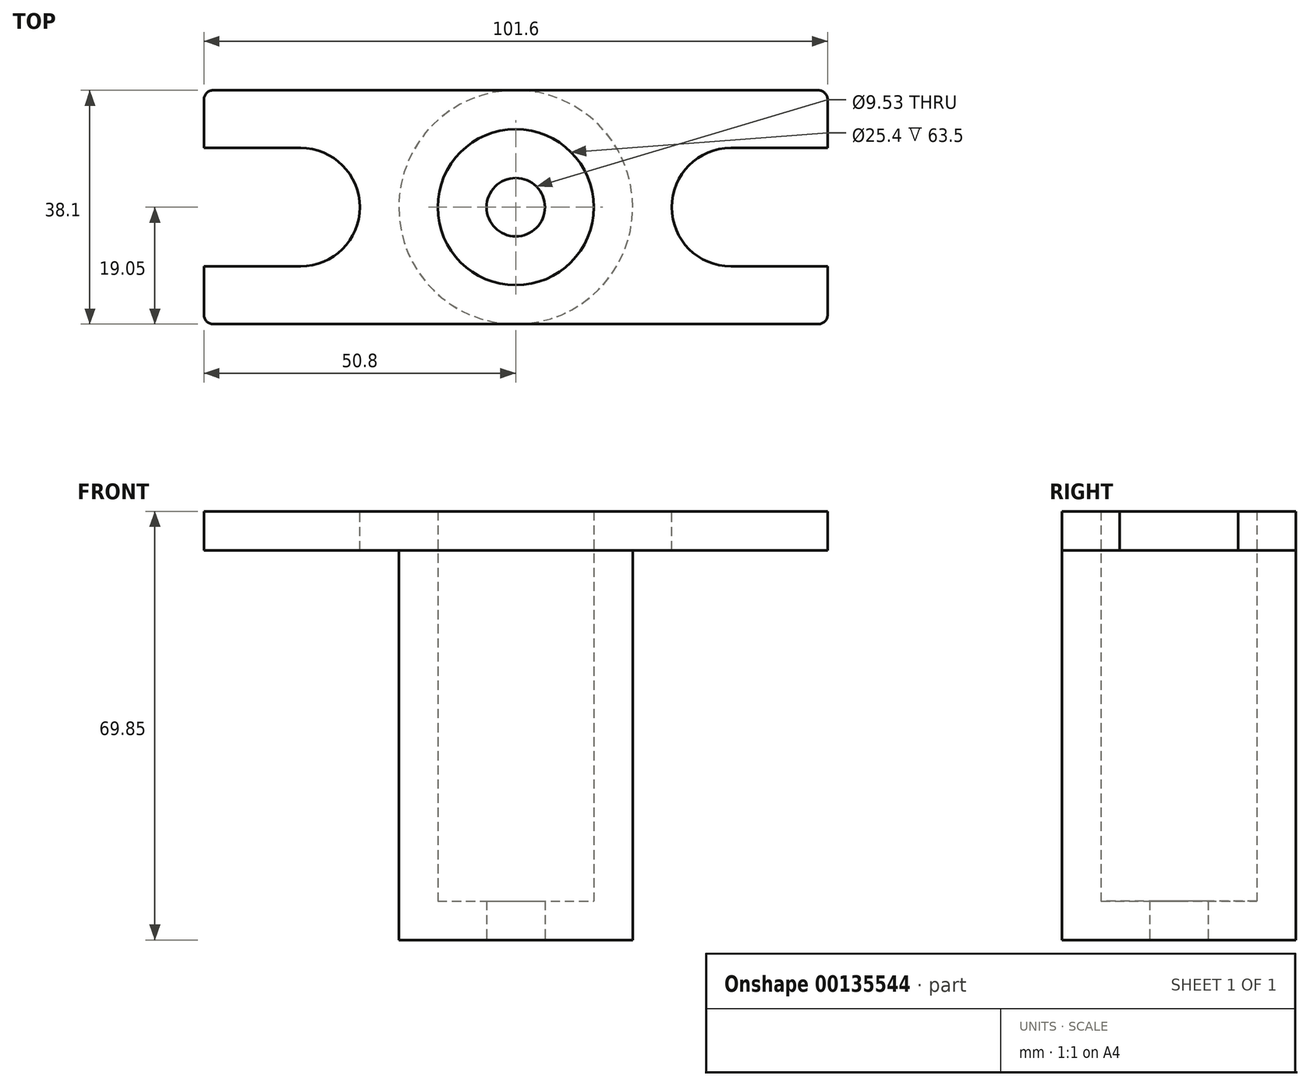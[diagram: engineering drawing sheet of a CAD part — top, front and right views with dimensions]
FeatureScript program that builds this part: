
annotation { "Feature Type Name" : "Feature", "Feature Type Description" : "" }
export const myFeature = defineFeature(function(context is Context, id is Id, definition is map)
    precondition{}
    {
        {
            var Q0;
            Q0=qCreatedBy(makeId("Front.planeOp"),FACE);
            var sketch = newSketch(context, id + "F0", { "sketchPlane" : qUnion([Q0])});
            skLineSegment(sketch, "E0", {"start": v(0, 0) * mm, "end": v(0, 62.9) * mm, "construction": true});
            skLineSegment(sketch, "E1", {"start": v(-4.76, 0) * mm, "end": v(-19.05, 0) * mm});
            skLineSegment(sketch, "E2", {"start": v(-19.05, 0) * mm, "end": v(-19.05, 69.85) * mm});
            skLineSegment(sketch, "E3", {"start": v(-19.05, 69.85) * mm, "end": v(-12.7, 69.85) * mm});
            skLineSegment(sketch, "E4", {"start": v(-12.7, 69.85) * mm, "end": v(-12.7, 6.35) * mm});
            skLineSegment(sketch, "E5", {"start": v(-12.7, 6.35) * mm, "end": v(-4.76, 6.35) * mm});
            skLineSegment(sketch, "E6", {"start": v(-4.76, 6.35) * mm, "end": v(-4.76, 0) * mm});
            skSolve(sketch);
        }
        {
            var Q0;
            Q0 = qSketchRegion(id + "F0", true);
            var Q1;
            Q1=sQuery(id+"F0.wireOp",EDGE,"E0");
            revolve(context, id + "F1", {"entities" : qUnion([Q0]), "axis" : qUnion([Q1]), "revolveType" : RevolveType.FULL});
        }
        {
            var Q0;
            Q0=makeQuery(id+"F1.opRevolve","SWEPT_FACE",FACE,{"disambiguationData":[OSD([sQuery(id+"F0.wireOp",EDGE,"E3")])]});
            var sketch = newSketch(context, id + "F2", { "sketchPlane" : qUnion([Q0])});
            skLineSegment(sketch, "E7.bottom", {"start": v(-49.28, 19.05) * mm, "end": v(49.28, 19.05) * mm});
            skLineSegment(sketch, "E7.top", {"start": v(-49.28, -19.05) * mm, "end": v(49.28, -19.05) * mm});
            skLineSegment(sketch, "E7.left", {"start": v(-50.8, 17.53) * mm, "end": v(-50.8, 9.65) * mm});
            skLineSegment(sketch, "E7.right", {"start": v(50.8, 17.53) * mm, "end": v(50.8, 9.65) * mm});
            skLineSegment(sketch, "E8", {"start": v(-50.8, 9.65) * mm, "end": v(-35.05, 9.65) * mm});
            skArc(sketch, "E9", {"start": v(-35.05, -9.65) * mm, "mid": v(-25.4, 0) * mm, "end": v(-35.05, 9.65) * mm});
            skLineSegment(sketch, "E10", {"start": v(-35.05, -9.65) * mm, "end": v(-50.8, -9.65) * mm});
            skLineSegment(sketch, "E11.trimOffspring", {"start": v(-50.8, -9.65) * mm, "end": v(-50.8, -17.53) * mm});
            skLineSegment(sketch, "E12", {"start": v(0, 25.68) * mm, "end": v(0, -43.56) * mm, "construction": true});
            skLineSegment(sketch, "E13.MirrorCS", {"start": v(35.05, -9.65) * mm, "end": v(50.8, -9.65) * mm});
            skLineSegment(sketch, "E14.MirrorCS", {"start": v(50.8, 9.65) * mm, "end": v(35.05, 9.65) * mm});
            skArc(sketch, "E15.MirrorCS", {"start": v(35.05, -9.65) * mm, "mid": v(25.4, 0) * mm, "end": v(35.05, 9.65) * mm});
            skLineSegment(sketch, "E16.trimOffspring", {"start": v(50.8, -9.65) * mm, "end": v(50.8, -17.53) * mm});
            skCircle(sketch, "E17.0", {"center": v(0, 0) * mm, "radius": 12.7 * mm});
            skPoint(sketch, "E18.visualSharp", {"position": v(-50.8, 19.05) * mm});
            skArc(sketch, "E18.filletArc", {"start": v(-49.28, 19.05) * mm, "mid": v(-50.35, 18.6) * mm, "end": v(-50.8, 17.53) * mm});
            skPoint(sketch, "E19.visualSharp", {"position": v(-50.8, -19.05) * mm});
            skArc(sketch, "E19.filletArc", {"start": v(-50.8, -17.53) * mm, "mid": v(-50.35, -18.6) * mm, "end": v(-49.28, -19.05) * mm});
            skPoint(sketch, "E20.visualSharp", {"position": v(50.8, 19.05) * mm});
            skArc(sketch, "E20.filletArc", {"start": v(50.8, 17.53) * mm, "mid": v(50.35, 18.6) * mm, "end": v(49.28, 19.05) * mm});
            skPoint(sketch, "E21.visualSharp", {"position": v(50.8, -19.05) * mm});
            skArc(sketch, "E21.filletArc", {"start": v(49.28, -19.05) * mm, "mid": v(50.35, -18.6) * mm, "end": v(50.8, -17.53) * mm});
            skSolve(sketch);
        }
        {
            var Q0;
            Q0 = qSketchRegion(id + "F2", true);
            extrude(context, id + "F3", {"entities" : qUnion([Q0]), "operationType" : NewBodyOperationType.ADD, "oppositeDirection" : true, "depth" : 6.35 * mm});
        }
    });
